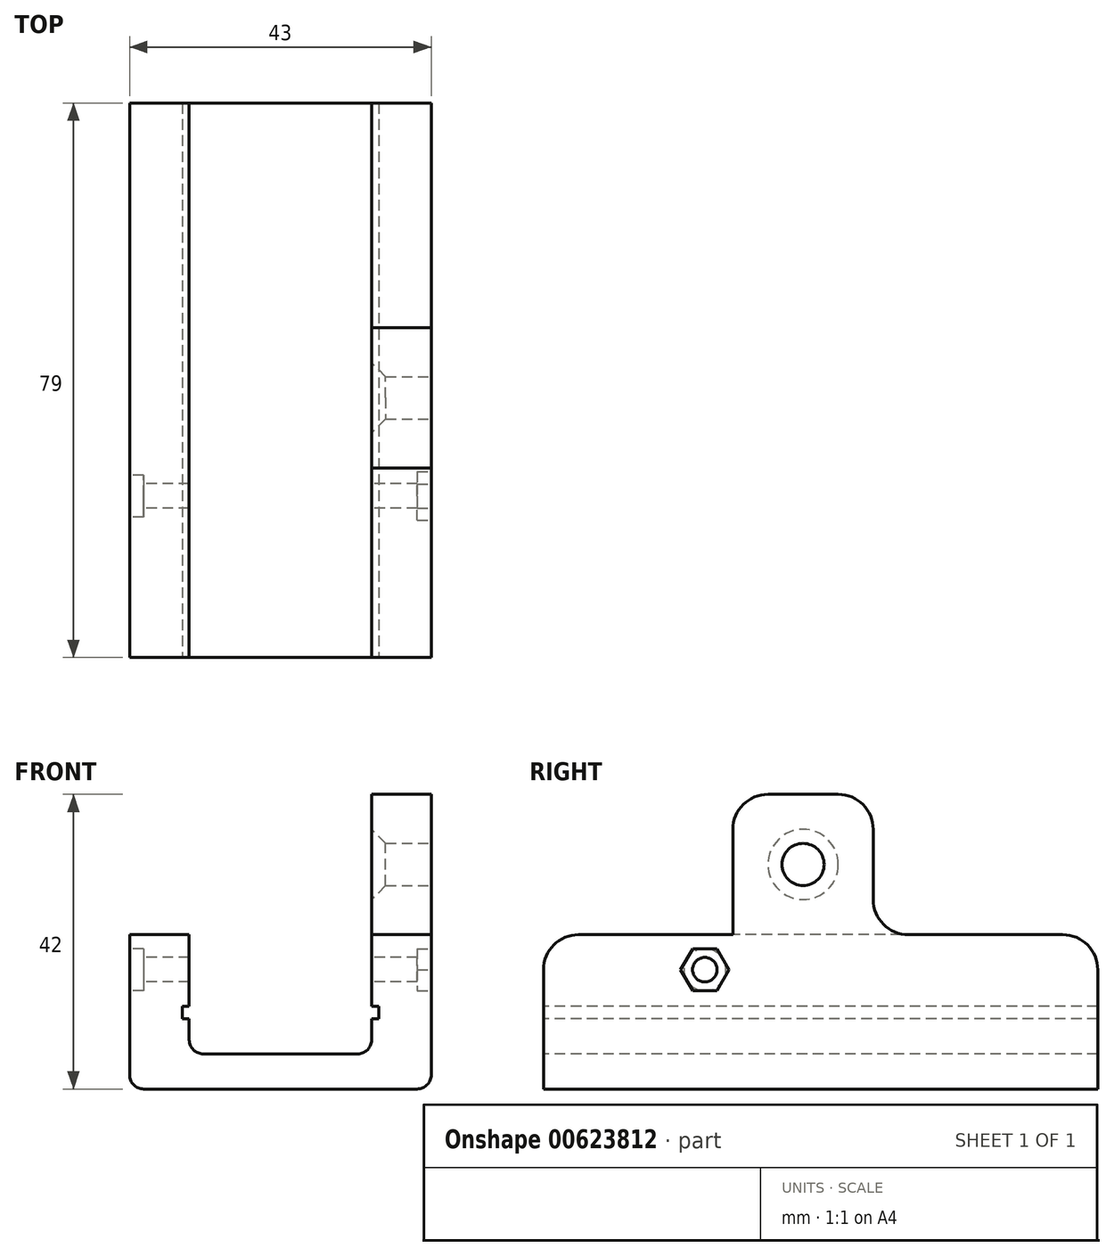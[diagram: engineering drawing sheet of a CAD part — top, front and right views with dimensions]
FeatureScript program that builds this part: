
annotation { "Feature Type Name" : "Feature", "Feature Type Description" : "" }
export const myFeature = defineFeature(function(context is Context, id is Id, definition is map)
    precondition{}
    {
        {
            var Q0;
            Q0=qCreatedBy(makeId("Top.planeOp"),FACE);
            var sketch = newSketch(context, id + "F0", { "sketchPlane" : qUnion([Q0])});
            skLineSegment(sketch, "E0.bottom", {"start": v(-14, 32) * mm, "end": v(14, 32) * mm});
            skLineSegment(sketch, "E0.top", {"start": v(-14, -32) * mm, "end": v(14, -32) * mm});
            skLineSegment(sketch, "E0.left", {"start": v(-14, 32) * mm, "end": v(-14, -32) * mm});
            skLineSegment(sketch, "E0.right", {"start": v(14, 32) * mm, "end": v(14, -32) * mm});
            skLineSegment(sketch, "E1.0", {"start": v(21.5, 39.5) * mm, "end": v(21.5, -39.5) * mm});
            skLineSegment(sketch, "E1.1", {"start": v(-21.5, 39.5) * mm, "end": v(21.5, 39.5) * mm});
            skLineSegment(sketch, "E1.2", {"start": v(-21.5, 39.5) * mm, "end": v(-21.5, -39.5) * mm});
            skLineSegment(sketch, "E1.3", {"start": v(-21.5, -39.5) * mm, "end": v(21.5, -39.5) * mm});
            skSolve(sketch);
        }
        {
            var Q0;
            Q0=makeQuery(id+"F0.imprint","IMPRINT",FACE,{"disambiguationData":[TD([[makeQuery(id+"F0.imprint","IMPRINT",EDGE,{"derivedFrom":sQuery(id+"F0.wireOp",EDGE,"E0.bottom")}),1.0]])]});
            var Q1;
            Q1=makeQuery(id+"F0.imprint","IMPRINT",FACE,{"disambiguationData":[TD([[makeQuery(id+"F0.imprint","IMPRINT",EDGE,{"derivedFrom":sQuery(id+"F0.wireOp",EDGE,"E0.bottom")}),-1.0]])]});
            extrude(context, id + "F1", {"entities" : qUnion([Q0, Q1]), "depth" : 22 * mm, "offsetDistance" : 25 * mm});
        }
        {
            var Q0;
            Q0=makeQuery(id+"F1.opExtrude","SWEPT_FACE",FACE,{"disambiguationData":[OSD([sQuery(id+"F0.wireOp",EDGE,"E1.3")])]});
            var sketch = newSketch(context, id + "F2", { "sketchPlane" : qUnion([Q0])});
            skLineSegment(sketch, "E2.bottom", {"start": v(-13, 22) * mm, "end": v(13, 22) * mm});
            skLineSegment(sketch, "E2.top", {"start": v(-13, 5) * mm, "end": v(13, 5) * mm});
            skLineSegment(sketch, "E2.left", {"start": v(-13, 22) * mm, "end": v(-13, 5) * mm});
            skLineSegment(sketch, "E2.right", {"start": v(13, 22) * mm, "end": v(13, 5) * mm});
            skLineSegment(sketch, "E3.bottom", {"start": v(-14, 11.8) * mm, "end": v(14, 11.8) * mm});
            skLineSegment(sketch, "E3.top", {"start": v(-14, 10) * mm, "end": v(14, 10) * mm});
            skLineSegment(sketch, "E3.left", {"start": v(-14, 11.8) * mm, "end": v(-14, 10) * mm});
            skLineSegment(sketch, "E3.right", {"start": v(14, 11.8) * mm, "end": v(14, 10) * mm});
            skSolve(sketch);
        }
        {
            var Q0;
            {var subQ0=sQuery(id+"F2.wireOp",EDGE,"E2.bottom");Q0=makeQuery(id+"F2.imprint","IMPRINT",FACE,{"disambiguationData":[TD([[makeQuery(id+"F2.imprint","IMPRINT",EDGE,{"derivedFrom":subQ0}),-1.0]])]});}
            var Q1;
            {var subQ0=sQuery(id+"F2.wireOp",EDGE,"E3.bottom");var subQ1=sQuery(id+"F2.wireOp",EDGE,"E2.left");var subQ2=makeQuery(id+"F2.imprint","INTERSECT",VERTEX,{"derivedFrom":[subQ1,subQ0]});Q1=makeQuery(id+"F2.imprint","IMPRINT",FACE,{"disambiguationData":[TD([[makeQuery(id+"F2.imprint","IMPRINT",EDGE,{"disambiguationData":[TD([[subQ2,-1.0]])],"derivedFrom":subQ1}),1.0]])]});}
            var Q2;
            {var subQ0=sQuery(id+"F2.wireOp",EDGE,"E2.top");Q2=makeQuery(id+"F2.imprint","IMPRINT",FACE,{"disambiguationData":[TD([[makeQuery(id+"F2.imprint","IMPRINT",EDGE,{"derivedFrom":subQ0}),1.0]])]});}
            var Q3;
            {var subQ5=sQuery(id+"F2.wireOp",EDGE,"E3.left");Q3=makeQuery(id+"F2.imprint","IMPRINT",FACE,{"disambiguationData":[TD([[makeQuery(id+"F2.imprint","IMPRINT",EDGE,{"derivedFrom":subQ5}),1.0]])]});}
            var Q4;
            {var subQ5=sQuery(id+"F2.wireOp",EDGE,"E3.right");Q4=makeQuery(id+"F2.imprint","IMPRINT",FACE,{"disambiguationData":[TD([[makeQuery(id+"F2.imprint","IMPRINT",EDGE,{"derivedFrom":subQ5}),-1.0]])]});}
            extrude(context, id + "F3", {"entities" : qUnion([Q0, Q1, Q2, Q3, Q4]), "operationType" : NewBodyOperationType.REMOVE, "oppositeDirection" : true, "depth" : 100 * mm, "offsetDistance" : 25 * mm});
        }
        {
            var Q0;
            Q0=makeQuery(id+"F1.opExtrude","SWEPT_FACE",FACE,{"disambiguationData":[OSD([sQuery(id+"F0.wireOp",EDGE,"E1.2")])]});
            var sketch = newSketch(context, id + "F4", { "sketchPlane" : qUnion([Q0])});
            skCircle(sketch, "E4", {"center": v(16.5, 17) * mm, "radius": 1.75 * mm});
            skCircle(sketch, "E5", {"center": v(16.5, 17) * mm, "radius": 3 * mm});
            skSolve(sketch);
        }
        {
            var Q0;
            Q0=makeQuery(id+"F4.imprint","IMPRINT",FACE,{"disambiguationData":[TD([[makeQuery(id+"F4.imprint","IMPRINT",EDGE,{"derivedFrom":sQuery(id+"F4.wireOp",EDGE,"E4")}),1.0]])]});
            extrude(context, id + "F5", {"entities" : qUnion([Q0]), "operationType" : NewBodyOperationType.REMOVE, "oppositeDirection" : true, "depth" : 100 * mm, "offsetDistance" : 25 * mm});
        }
        {
            var Q0;
            Q0=makeQuery(id+"F4.imprint","IMPRINT",FACE,{"disambiguationData":[TD([[makeQuery(id+"F4.imprint","IMPRINT",EDGE,{"derivedFrom":sQuery(id+"F4.wireOp",EDGE,"E4")}),-1.0]])]});
            extrude(context, id + "F6", {"entities" : qUnion([Q0]), "operationType" : NewBodyOperationType.REMOVE, "oppositeDirection" : true, "depth" : 2 * mm, "offsetDistance" : 25 * mm});
        }
        {
            var Q0;
            Q0=makeQuery(id+"F1.opExtrude","SWEPT_FACE",FACE,{"disambiguationData":[OSD([sQuery(id+"F0.wireOp",EDGE,"E1.0")])]});
            var sketch = newSketch(context, id + "F7", { "sketchPlane" : qUnion([Q0])});
            skCircle(sketch, "E6.cCircle", {"center": v(-16.5, 17) * mm, "radius": 3 * mm, "construction": true});
            skLineSegment(sketch, "E6.0", {"start": v(-14.77, 14) * mm, "end": v(-18.23, 14) * mm});
            skLineSegment(sketch, "E6.1", {"start": v(-18.23, 14) * mm, "end": v(-19.96, 17) * mm});
            skLineSegment(sketch, "E6.2", {"start": v(-19.96, 17) * mm, "end": v(-18.23, 20) * mm});
            skLineSegment(sketch, "E6.3", {"start": v(-18.23, 20) * mm, "end": v(-14.77, 20) * mm});
            skLineSegment(sketch, "E6.4", {"start": v(-14.77, 20) * mm, "end": v(-13.04, 17) * mm});
            skLineSegment(sketch, "E6.5", {"start": v(-13.04, 17) * mm, "end": v(-14.77, 14) * mm});
            skPoint(sketch, "E6.0.midPoint", {"position": v(-16.5, 14) * mm});
            skSolve(sketch);
        }
        {
            var Q0;
            Q0=makeQuery(id+"F7.imprint","IMPRINT",FACE,{"disambiguationData":[TD([[makeQuery(id+"F7.imprint","IMPRINT",EDGE,{"derivedFrom":sQuery(id+"F7.wireOp",EDGE,"E6.0")}),-1.0]])]});
            extrude(context, id + "F8", {"entities" : qUnion([Q0]), "operationType" : NewBodyOperationType.REMOVE, "oppositeDirection" : true, "depth" : 2 * mm, "offsetDistance" : 25 * mm});
        }
        {
            var Q0;
            {var subQ0=sQuery(id+"F0.wireOp",EDGE,"E1.0");var subQ1=sQuery(id+"F0.wireOp",EDGE,"E1.3");var subQ3=sQuery(id+"F0.wireOp",EDGE,"E1.1");Q0=makeQuery(id+"F3.boolean.opBoolean","SPLIT",FACE,{"disambiguationData":[TD([makeQuery(id+"F1.opExtrude","SWEPT_FACE",FACE,{"disambiguationData":[OSD([subQ0])]})])],"derivedFrom":makeQuery(id+"F1.opExtrude","CAP_FACE",FACE,{"disambiguationData":[OSD([subQ0,subQ3,sQuery(id+"F0.wireOp",EDGE,"E1.2"),subQ1])],"isStart":false})});}
            var sketch = newSketch(context, id + "F9", { "sketchPlane" : qUnion([Q0])});
            skLineSegment(sketch, "E7.bottom", {"start": v(13, -12.5) * mm, "end": v(21.5, -12.5) * mm});
            skLineSegment(sketch, "E7.top", {"start": v(13, 7.5) * mm, "end": v(21.5, 7.5) * mm});
            skLineSegment(sketch, "E7.left", {"start": v(13, -12.5) * mm, "end": v(13, 7.5) * mm});
            skLineSegment(sketch, "E7.right", {"start": v(21.5, -12.5) * mm, "end": v(21.5, 7.5) * mm});
            skSolve(sketch);
        }
        {
            var Q0;
            Q0=makeQuery(id+"F9.imprint","IMPRINT",FACE,{"disambiguationData":[TD([[makeQuery(id+"F9.imprint","IMPRINT",EDGE,{"derivedFrom":sQuery(id+"F9.wireOp",EDGE,"Y789hdBv-wxHL-dYbn-I5PN-ZGRhep4BcXWg.bottom")}),1.0]])]});
            var Q1;
            Q1=makeQuery(id+"F9.imprint","IMPRINT",FACE,{"disambiguationData":[TD([[makeQuery(id+"F9.imprint","IMPRINT",EDGE,{"derivedFrom":sQuery(id+"F9.wireOp",EDGE,"E7.bottom")}),1.0]])]});
            extrude(context, id + "F10", {"entities" : qUnion([Q0, Q1]), "operationType" : NewBodyOperationType.ADD, "depth" : 20 * mm, "offsetDistance" : 25 * mm});
        }
        {
            var Q0;
            Q0=makeQuery(id+"F10.boolean.opBoolean","MERGE",FACE,{"derivedFrom":[makeQuery(id+"F1.opExtrude","SWEPT_FACE",FACE,{"disambiguationData":[OSD([sQuery(id+"F0.wireOp",EDGE,"E1.0")])]}),makeQuery(id+"F10.opExtrude","SWEPT_FACE",FACE,{"disambiguationData":[OSD([sQuery(id+"F9.wireOp",EDGE,"E7.right")])]})]});
            var sketch = newSketch(context, id + "F11", { "sketchPlane" : qUnion([Q0])});
            skCircle(sketch, "E8", {"center": v(-2.5, 32) * mm, "radius": 3 * mm});
            skPoint(sketch, "E8.centerSnap0", {"position": v(-2.5, 42) * mm});
            skPoint(sketch, "E8.centerSnap1", {"position": v(-12.5, 32) * mm});
            skSolve(sketch);
        }
        {
            var Q0;
            Q0=makeQuery(id+"F11.imprint","IMPRINT",FACE,{"disambiguationData":[TD([[makeQuery(id+"F11.imprint","IMPRINT",EDGE,{"derivedFrom":sQuery(id+"F11.wireOp",EDGE,"E8")}),1.0]])]});
            extrude(context, id + "F12", {"entities" : qUnion([Q0]), "operationType" : NewBodyOperationType.REMOVE, "oppositeDirection" : true, "depth" : 25 * mm, "offsetDistance" : 25 * mm});
        }
        {
            var Q0;
            {var subQ0=sQuery(id+"F2.wireOp",EDGE,"E2.right");Q0=makeQuery(id+"F12.boolean.opBoolean","INTERSECT",EDGE,{"derivedFrom":[makeQuery(id+"F10.boolean.opBoolean","MERGE",FACE,{"derivedFrom":[makeQuery(id+"F3.boolean.opBoolean","COPY",FACE,{"derivedFrom":makeQuery(id+"F3.opExtrude","SWEPT_FACE",FACE,{"disambiguationData":[OSD([subQ0]),TDD([makeQuery(id+"F2.imprint","IMPRINT",EDGE,{"disambiguationData":[TD([[makeQuery(id+"F2.imprint","INTERSECT",VERTEX,{"derivedFrom":[subQ0,sQuery(id+"F2.wireOp",EDGE,"E3.bottom")]}),1.0]])],"derivedFrom":subQ0})])]})}),makeQuery(id+"F10.opExtrude","SWEPT_FACE",FACE,{"disambiguationData":[OSD([sQuery(id+"F9.wireOp",EDGE,"E7.left")])]})]}),makeQuery(id+"F12.opExtrude","SWEPT_FACE",FACE,{"disambiguationData":[OSD([sQuery(id+"F11.wireOp",EDGE,"E8")])]})]});}
            chamfer(context, id + "F13", {"entities" : qUnion([Q0]), "width" : 2 * mm, "tangentPropagation" : true});
        }
        {
            var Q0;
            Q0=makeQuery(id+"F10.opExtrude","CAP_EDGE",EDGE,{"disambiguationData":[OSD([sQuery(id+"F9.wireOp",EDGE,"E7.top")])],"isStart":false});
            var Q1;
            Q1=makeQuery(id+"F10.opExtrude","CAP_EDGE",EDGE,{"disambiguationData":[OSD([sQuery(id+"F9.wireOp",EDGE,"E7.bottom")])],"isStart":false});
            var Q2;
            Q2=makeQuery(id+"F10.opExtrude","CAP_EDGE",EDGE,{"disambiguationData":[OSD([sQuery(id+"F9.wireOp",EDGE,"E7.bottom")])],"isStart":true});
            var Q3;
            Q3=makeQuery(id+"F10.opExtrude","CAP_EDGE",EDGE,{"disambiguationData":[OSD([sQuery(id+"F9.wireOp",EDGE,"E7.top")])],"isStart":true});
            var Q4;
            {var subQ0=sQuery(id+"F0.wireOp",EDGE,"E1.0");var subQ3=sQuery(id+"F0.wireOp",EDGE,"E1.1");Q4=makeQuery(id+"F3.boolean.opBoolean","SPLIT",EDGE,{"disambiguationData":[TD([makeQuery(id+"F1.opExtrude","SWEPT_FACE",FACE,{"disambiguationData":[OSD([subQ0])]})])],"derivedFrom":makeQuery(id+"F1.opExtrude","CAP_EDGE",EDGE,{"disambiguationData":[OSD([subQ3])],"isStart":false})});}
            var Q5;
            {var subQ0=sQuery(id+"F0.wireOp",EDGE,"E1.0");var subQ1=sQuery(id+"F0.wireOp",EDGE,"E1.3");var subQ3=makeQuery(id+"F1.opExtrude","CAP_EDGE",EDGE,{"disambiguationData":[OSD([subQ1])],"isStart":false});Q5=makeQuery(id+"F3.boolean.opBoolean","SPLIT",EDGE,{"disambiguationData":[TD([makeQuery(id+"F1.opExtrude","SWEPT_FACE",FACE,{"disambiguationData":[OSD([subQ0])]})])],"derivedFrom":subQ3});}
            var Q6;
            {var subQ0=sQuery(id+"F0.wireOp",EDGE,"E1.3");var subQ1=sQuery(id+"F0.wireOp",EDGE,"E1.2");var subQ3=makeQuery(id+"F1.opExtrude","CAP_EDGE",EDGE,{"disambiguationData":[OSD([subQ0])],"isStart":false});Q6=makeQuery(id+"F3.boolean.opBoolean","SPLIT",EDGE,{"disambiguationData":[TD([makeQuery(id+"F1.opExtrude","SWEPT_FACE",FACE,{"disambiguationData":[OSD([subQ1])]})])],"derivedFrom":subQ3});}
            var Q7;
            {var subQ1=sQuery(id+"F0.wireOp",EDGE,"E1.2");var subQ2=sQuery(id+"F0.wireOp",EDGE,"E1.1");Q7=makeQuery(id+"F3.boolean.opBoolean","SPLIT",EDGE,{"disambiguationData":[TD([makeQuery(id+"F1.opExtrude","SWEPT_FACE",FACE,{"disambiguationData":[OSD([subQ1])]})])],"derivedFrom":makeQuery(id+"F1.opExtrude","CAP_EDGE",EDGE,{"disambiguationData":[OSD([subQ2])],"isStart":false})});}
            fillet(context, id + "F14", {"entities" : qUnion([Q0, Q1, Q2, Q3, Q4, Q5, Q6, Q7]), "radius" : 5 * mm, "tangentPropagation" : true, "allowEdgeOverflow" : false});
        }
        {
            var Q0;
            Q0=makeQuery(id+"F3.boolean.opBoolean","COPY",EDGE,{"derivedFrom":makeQuery(id+"F3.opExtrude","SWEPT_EDGE",EDGE,{"disambiguationData":[OSD([sQuery(id+"F2.wireOp",EDGE,"E2.top"),sQuery(id+"F2.wireOp",EDGE,"E2.right")])]})});
            var Q1;
            Q1=makeQuery(id+"F3.boolean.opBoolean","COPY",EDGE,{"derivedFrom":makeQuery(id+"F3.opExtrude","SWEPT_EDGE",EDGE,{"disambiguationData":[OSD([sQuery(id+"F2.wireOp",EDGE,"E2.top"),sQuery(id+"F2.wireOp",EDGE,"E2.left")])]})});
            var Q2;
            Q2=makeQuery(id+"F1.opExtrude","CAP_EDGE",EDGE,{"disambiguationData":[OSD([sQuery(id+"F0.wireOp",EDGE,"E1.0")])],"isStart":true});
            var Q3;
            Q3=makeQuery(id+"F1.opExtrude","CAP_EDGE",EDGE,{"disambiguationData":[OSD([sQuery(id+"F0.wireOp",EDGE,"E1.2")])],"isStart":true});
            fillet(context, id + "F15", {"entities" : qUnion([Q0, Q1, Q2, Q3]), "radius" : 2 * mm, "tangentPropagation" : true, "allowEdgeOverflow" : false});
        }
    });
